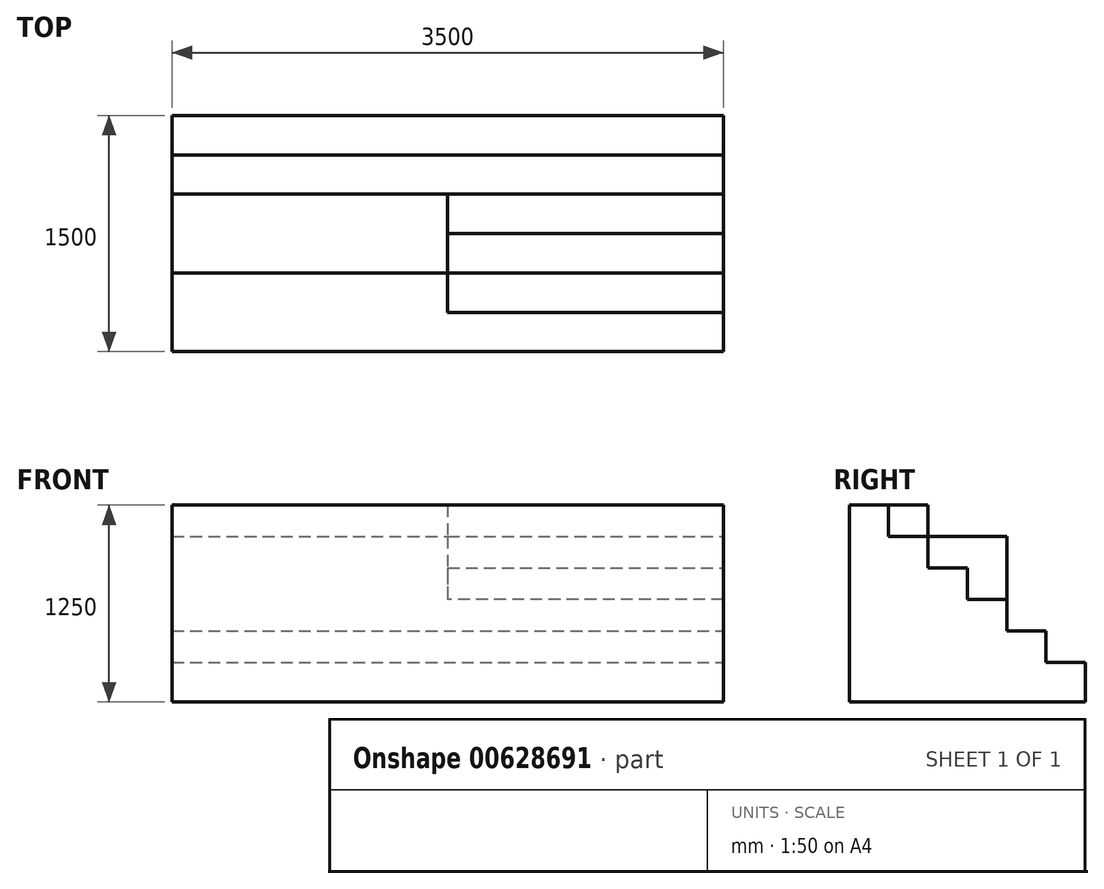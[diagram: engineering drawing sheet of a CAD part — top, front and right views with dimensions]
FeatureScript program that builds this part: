
annotation { "Feature Type Name" : "Feature", "Feature Type Description" : "" }
export const myFeature = defineFeature(function(context is Context, id is Id, definition is map)
    precondition{}
    {
        {
            var Q0;
            Q0=qCreatedBy(makeId("Top.planeOp"),FACE);
            var sketch = newSketch(context, id + "F0", { "sketchPlane" : qUnion([Q0])});
            skLineSegment(sketch, "E0.bottom", {"start": v(0, 0) * mm, "end": v(3500, 0) * mm});
            skLineSegment(sketch, "E0.top", {"start": v(0, 1500) * mm, "end": v(3500, 1500) * mm});
            skLineSegment(sketch, "E0.left", {"start": v(0, 0) * mm, "end": v(0, 1500) * mm});
            skLineSegment(sketch, "E0.right", {"start": v(3500, 0) * mm, "end": v(3500, 1500) * mm});
            skSolve(sketch);
        }
        {
            var Q0;
            Q0=makeQuery(id+"F0.imprint","IMPRINT",FACE,{"disambiguationData":[TD([[makeQuery(id+"F0.imprint","IMPRINT",EDGE,{"derivedFrom":sQuery(id+"F0.wireOp",EDGE,"E0.bottom")}),1.0]])]});
            extrude(context, id + "F1", {"entities" : qUnion([Q0]), "depth" : 250 * mm, "offsetDistance" : 25 * mm});
        }
        {
            var Q0;
            Q0=makeQuery(id+"F1.opExtrude","CAP_FACE",FACE,{"disambiguationData":[OSD([sQuery(id+"F0.wireOp",EDGE,"E0.bottom"),sQuery(id+"F0.wireOp",EDGE,"E0.top"),sQuery(id+"F0.wireOp",EDGE,"E0.left"),sQuery(id+"F0.wireOp",EDGE,"E0.right")])],"isStart":false});
            var sketch = newSketch(context, id + "F2", { "sketchPlane" : qUnion([Q0])});
            skLineSegment(sketch, "E1.bottom", {"start": v(0, 0) * mm, "end": v(3500, 0) * mm});
            skLineSegment(sketch, "E1.top", {"start": v(0, 1250) * mm, "end": v(3500, 1250) * mm});
            skLineSegment(sketch, "E1.left", {"start": v(0, 0) * mm, "end": v(0, 1250) * mm});
            skLineSegment(sketch, "E1.right", {"start": v(3500, 0) * mm, "end": v(3500, 1250) * mm});
            skSolve(sketch);
        }
        {
            var Q0;
            Q0=makeQuery(id+"F2.imprint","IMPRINT",FACE,{"disambiguationData":[TD([[makeQuery(id+"F2.imprint","IMPRINT",EDGE,{"derivedFrom":sQuery(id+"F2.wireOp",EDGE,"E1.bottom")}),1.0]])]});
            extrude(context, id + "F3", {"entities" : qUnion([Q0]), "operationType" : NewBodyOperationType.ADD, "depth" : 200 * mm, "offsetDistance" : 25 * mm});
        }
        {
            var Q0;
            Q0=makeQuery(id+"F3.opExtrude","CAP_FACE",FACE,{"disambiguationData":[OSD([sQuery(id+"F2.wireOp",EDGE,"E1.bottom"),sQuery(id+"F2.wireOp",EDGE,"E1.top"),sQuery(id+"F2.wireOp",EDGE,"E1.left"),sQuery(id+"F2.wireOp",EDGE,"E1.right")])],"isStart":false});
            var sketch = newSketch(context, id + "F4", { "sketchPlane" : qUnion([Q0])});
            skLineSegment(sketch, "E2.bottom", {"start": v(0, 0) * mm, "end": v(1750, 0) * mm});
            skLineSegment(sketch, "E2.top", {"start": v(0, 500) * mm, "end": v(1750, 500) * mm});
            skLineSegment(sketch, "E2.left", {"start": v(0, 0) * mm, "end": v(0, 500) * mm});
            skLineSegment(sketch, "E2.right", {"start": v(1750, 0) * mm, "end": v(1750, 500) * mm});
            skLineSegment(sketch, "E3.bottom", {"start": v(1750, 0) * mm, "end": v(3500, 0) * mm});
            skLineSegment(sketch, "E3.top", {"start": v(1750, 250) * mm, "end": v(3500, 250) * mm});
            skLineSegment(sketch, "E3.left", {"start": v(1750, 0) * mm, "end": v(1750, 250) * mm});
            skLineSegment(sketch, "E3.right", {"start": v(3500, 0) * mm, "end": v(3500, 250) * mm});
            skSolve(sketch);
        }
        {
            var Q0;
            Q0=makeQuery(id+"F4.imprint","IMPRINT",FACE,{"disambiguationData":[TD([[makeQuery(id+"F4.imprint","IMPRINT",EDGE,{"derivedFrom":sQuery(id+"F4.wireOp",EDGE,"E2.bottom")}),1.0]])]});
            var Q1;
            Q1=makeQuery(id+"F4.imprint","IMPRINT",FACE,{"disambiguationData":[TD([[makeQuery(id+"F4.imprint","IMPRINT",EDGE,{"derivedFrom":sQuery(id+"F4.wireOp",EDGE,"E3.bottom")}),1.0]])]});
            extrude(context, id + "F5", {"entities" : qUnion([Q0, Q1]), "operationType" : NewBodyOperationType.ADD, "depth" : 800 * mm, "offsetDistance" : 25 * mm});
        }
        {
            var Q0;
            Q0=makeQuery(id+"F3.opExtrude","CAP_FACE",FACE,{"disambiguationData":[OSD([sQuery(id+"F2.wireOp",EDGE,"E1.bottom"),sQuery(id+"F2.wireOp",EDGE,"E1.top"),sQuery(id+"F2.wireOp",EDGE,"E1.left"),sQuery(id+"F2.wireOp",EDGE,"E1.right")])],"isStart":false});
            var sketch = newSketch(context, id + "F6", { "sketchPlane" : qUnion([Q0])});
            skLineSegment(sketch, "E4.bottom", {"start": v(1750, 500) * mm, "end": v(3500, 500) * mm});
            skLineSegment(sketch, "E4.top", {"start": v(1750, 250) * mm, "end": v(3500, 250) * mm});
            skLineSegment(sketch, "E4.left", {"start": v(1750, 500) * mm, "end": v(1750, 250) * mm});
            skLineSegment(sketch, "E4.right", {"start": v(3500, 500) * mm, "end": v(3500, 250) * mm});
            skLineSegment(sketch, "E5.bottom", {"start": v(0, 1000) * mm, "end": v(1750, 1000) * mm});
            skLineSegment(sketch, "E5.top", {"start": v(0, 500) * mm, "end": v(1750, 500) * mm});
            skLineSegment(sketch, "E5.left", {"start": v(0, 1000) * mm, "end": v(0, 500) * mm});
            skLineSegment(sketch, "E5.right", {"start": v(1750, 1000) * mm, "end": v(1750, 500) * mm});
            skSolve(sketch);
        }
        {
            var Q0;
            Q0=makeQuery(id+"F6.imprint","IMPRINT",FACE,{"disambiguationData":[TD([[makeQuery(id+"F6.imprint","IMPRINT",EDGE,{"derivedFrom":sQuery(id+"F6.wireOp",EDGE,"E5.bottom")}),-1.0]])]});
            var Q1;
            Q1=makeQuery(id+"F6.imprint","IMPRINT",FACE,{"disambiguationData":[TD([[makeQuery(id+"F6.imprint","IMPRINT",EDGE,{"derivedFrom":sQuery(id+"F6.wireOp",EDGE,"E4.bottom")}),-1.0]])]});
            extrude(context, id + "F7", {"entities" : qUnion([Q0, Q1]), "operationType" : NewBodyOperationType.ADD, "depth" : 600 * mm, "offsetDistance" : 25 * mm});
        }
        {
            var Q0;
            Q0=makeQuery(id+"F3.opExtrude","CAP_FACE",FACE,{"disambiguationData":[OSD([sQuery(id+"F2.wireOp",EDGE,"E1.bottom"),sQuery(id+"F2.wireOp",EDGE,"E1.top"),sQuery(id+"F2.wireOp",EDGE,"E1.left"),sQuery(id+"F2.wireOp",EDGE,"E1.right")])],"isStart":false});
            var sketch = newSketch(context, id + "F8", { "sketchPlane" : qUnion([Q0])});
            skLineSegment(sketch, "E6.bottom", {"start": v(1750, 500) * mm, "end": v(3500, 500) * mm});
            skLineSegment(sketch, "E6.top", {"start": v(1750, 750) * mm, "end": v(3500, 750) * mm});
            skLineSegment(sketch, "E6.left", {"start": v(1750, 500) * mm, "end": v(1750, 750) * mm});
            skLineSegment(sketch, "E6.right", {"start": v(3500, 500) * mm, "end": v(3500, 750) * mm});
            skSolve(sketch);
        }
        {
            var Q0;
            Q0=makeQuery(id+"F8.imprint","IMPRINT",FACE,{"disambiguationData":[TD([[makeQuery(id+"F8.imprint","IMPRINT",EDGE,{"derivedFrom":sQuery(id+"F8.wireOp",EDGE,"E6.bottom")}),1.0]])]});
            extrude(context, id + "F9", {"entities" : qUnion([Q0]), "operationType" : NewBodyOperationType.ADD, "depth" : 400 * mm, "offsetDistance" : 25 * mm});
        }
        {
            var Q0;
            Q0=makeQuery(id+"F3.opExtrude","CAP_FACE",FACE,{"disambiguationData":[OSD([sQuery(id+"F2.wireOp",EDGE,"E1.bottom"),sQuery(id+"F2.wireOp",EDGE,"E1.top"),sQuery(id+"F2.wireOp",EDGE,"E1.left"),sQuery(id+"F2.wireOp",EDGE,"E1.right")])],"isStart":false});
            var sketch = newSketch(context, id + "F10", { "sketchPlane" : qUnion([Q0])});
            skLineSegment(sketch, "E7.bottom", {"start": v(3500, 750) * mm, "end": v(1750, 750) * mm});
            skLineSegment(sketch, "E7.top", {"start": v(3500, 1000) * mm, "end": v(1750, 1000) * mm});
            skLineSegment(sketch, "E7.left", {"start": v(3500, 750) * mm, "end": v(3500, 1000) * mm});
            skLineSegment(sketch, "E7.right", {"start": v(1750, 750) * mm, "end": v(1750, 1000) * mm});
            skSolve(sketch);
        }
        {
            var Q0;
            Q0=makeQuery(id+"F10.imprint","IMPRINT",FACE,{"disambiguationData":[TD([[makeQuery(id+"F10.imprint","IMPRINT",EDGE,{"derivedFrom":sQuery(id+"F10.wireOp",EDGE,"E7.bottom")}),1.0]])]});
            extrude(context, id + "F11", {"entities" : qUnion([Q0]), "operationType" : NewBodyOperationType.ADD, "depth" : 200 * mm, "offsetDistance" : 25 * mm});
        }
    });
